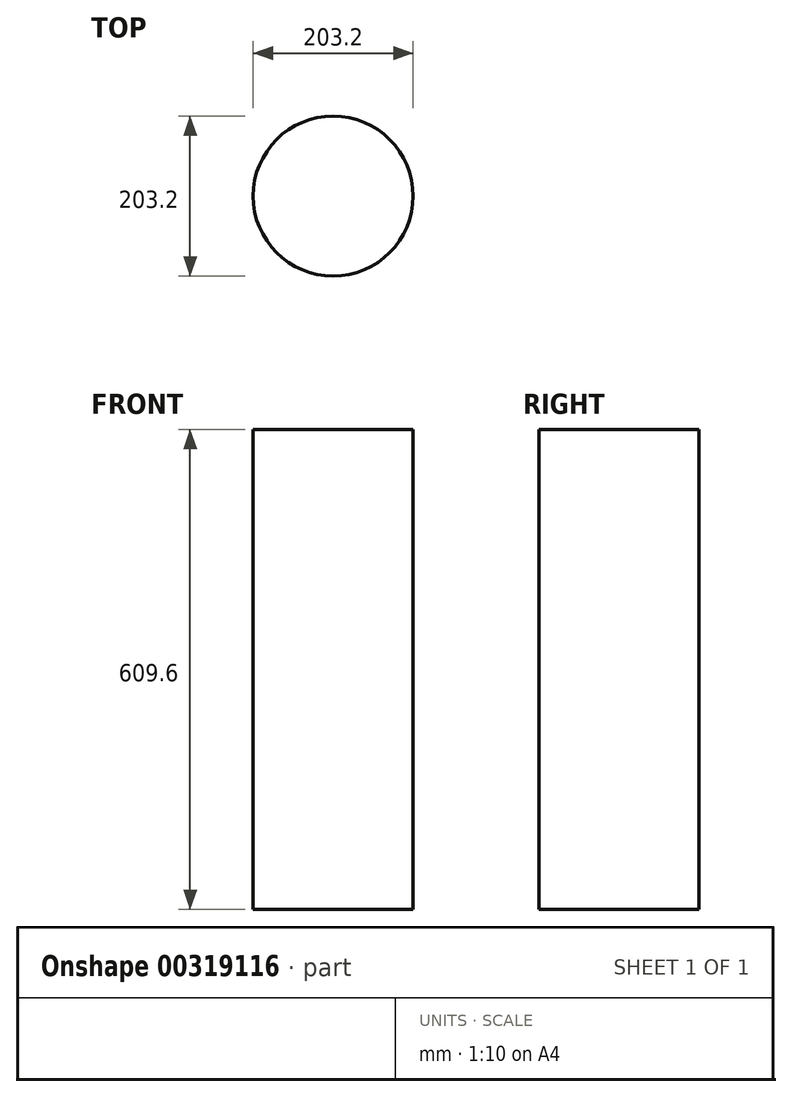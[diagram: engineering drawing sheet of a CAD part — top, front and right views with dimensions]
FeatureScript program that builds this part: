
annotation { "Feature Type Name" : "Feature", "Feature Type Description" : "" }
export const myFeature = defineFeature(function(context is Context, id is Id, definition is map)
    precondition{}
    {
        {
            var Q0;
            Q0=qCreatedBy(makeId("Front.planeOp"),FACE);
            var sketch = newSketch(context, id + "F0", { "sketchPlane" : qUnion([Q0])});
            skLineSegment(sketch, "E0.bottom", {"start": v(-101.6, 443.7) * mm, "end": v(0, 443.7) * mm});
            skLineSegment(sketch, "E0.top", {"start": v(-101.6, -165.9) * mm, "end": v(0, -165.9) * mm});
            skLineSegment(sketch, "E0.left", {"start": v(-101.6, 443.7) * mm, "end": v(-101.6, -165.9) * mm});
            skLineSegment(sketch, "E0.right", {"start": v(0, 443.7) * mm, "end": v(0, -165.9) * mm});
            skSolve(sketch);
        }
        {
            var Q0;
            Q0=makeQuery(id+"F0.imprint","IMPRINT",FACE,{"disambiguationData":[TD([[makeQuery(id+"F0.imprint","IMPRINT",EDGE,{"derivedFrom":sQuery(id+"F0.wireOp",EDGE,"E0.bottom")}),-1.0]])]});
            var Q1;
            Q1=sQuery(id+"F0.wireOp",EDGE,"E0.right");
            revolve(context, id + "F1", {"entities" : qUnion([Q0]), "axis" : qUnion([Q1]), "revolveType" : RevolveType.FULL});
        }
    });
